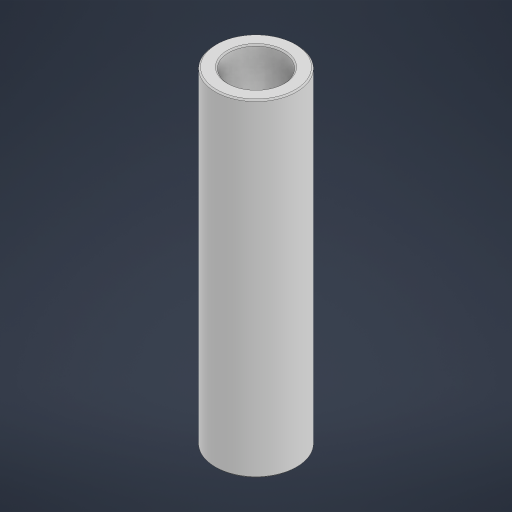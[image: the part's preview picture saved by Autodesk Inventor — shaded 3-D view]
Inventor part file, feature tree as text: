
AUTODESK INVENTOR PART (.ipt)
format: ipt  version: 2023 (Build 270158000, 158)  size: 177,152 bytes
history: native  units: in
note: dims shown in document units (in); Inventor stores cm internally (conversion verified against a paired STEP export)
features: chamfer x1
ambient origin geometry x8: Origin, YZ Plane, XZ Plane, XY Plane, X Axis, Y Axis, Z Axis, Center Point
bodies: Solid1 (feature_tree)
feature tree (1):
  chamfer  "Chamfer1"  [1 undecoded]
note: 1 required parameter value undecoded (feature->parameter linkage not recoverable at this tier; creation-order binding heuristic only, values carry confidence <= 0.55)
